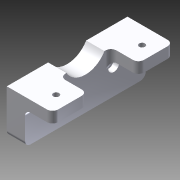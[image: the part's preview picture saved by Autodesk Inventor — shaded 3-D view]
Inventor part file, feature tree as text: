
AUTODESK INVENTOR PART (.ipt)
format: ipt  version: 2015 SP1 (Build 190203100, 203)  size: 185,344 bytes
history: native  units: mm
features: sketch x6, reference x5, extrude x4, fillet x2, hole x2, projected_geometry x1
ambient origin geometry x8: Origin, YZ Plane, XZ Plane, XY Plane, X Axis, Y Axis, Z Axis, Center Point
bodies: Solid1 (feature_tree)
feature tree (20):
  extrude  "Extrusion1"  Depth=24.0mm
  fillet  "Fillet1"  Radius=24.0mm
  extrude  "Extrusion2"  Depth=3.0mm
  hole  "Hole2"  [1 undecoded]
  hole  "Hole3"  [1 undecoded]
  extrude  "Extrusion4"  Depth=10.0mm
  fillet  "Fillet4"  Radius=5.6mm
  extrude  "Extrusion5"  Depth=3.0mm TaperAngle=0.0deg
  sketch  "Sketch1"  dims[d0=10.0mm d1=66.0mm d2=24.0mm d3=0.0mm]
  sketch  "Sketch2"  dims[d4=3.0mm d5=6.0mm]
  projected_geometry  "Projected Loop1"
  sketch  "Sketch5"  dims[d6=19.0mm d7=6.0mm]
  reference  "Reference1"
  reference  "Reference2"
  sketch  "Sketch6"  dims[d8=19.0mm d9=15.0mm d10=0.0mm]
  reference  "Reference3"
  reference  "Reference4"
  sketch  "Sketch7"  dims[d26=3.2mm d27=6.0mm d28=6.0mm d29=3.0mm d30=90.0deg d31=8.0mm d32=20.594885mm]
  sketch  "Sketch8"  dims[d33=3.2mm d34=6.0mm d35=6.0mm d36=3.0mm d37=90.0deg d38=8.0mm d39=20.594885mm d40=5.6mm d41=5.6mm d42=3.0mm d43=0.0mm d44=3.0mm d45=1.0mm d46=10.0mm d47=0.0mm]
  reference  "Reference5"
note: 2 required parameter values undecoded (feature->parameter linkage not recoverable at this tier; creation-order binding heuristic only, values carry confidence <= 0.55)
